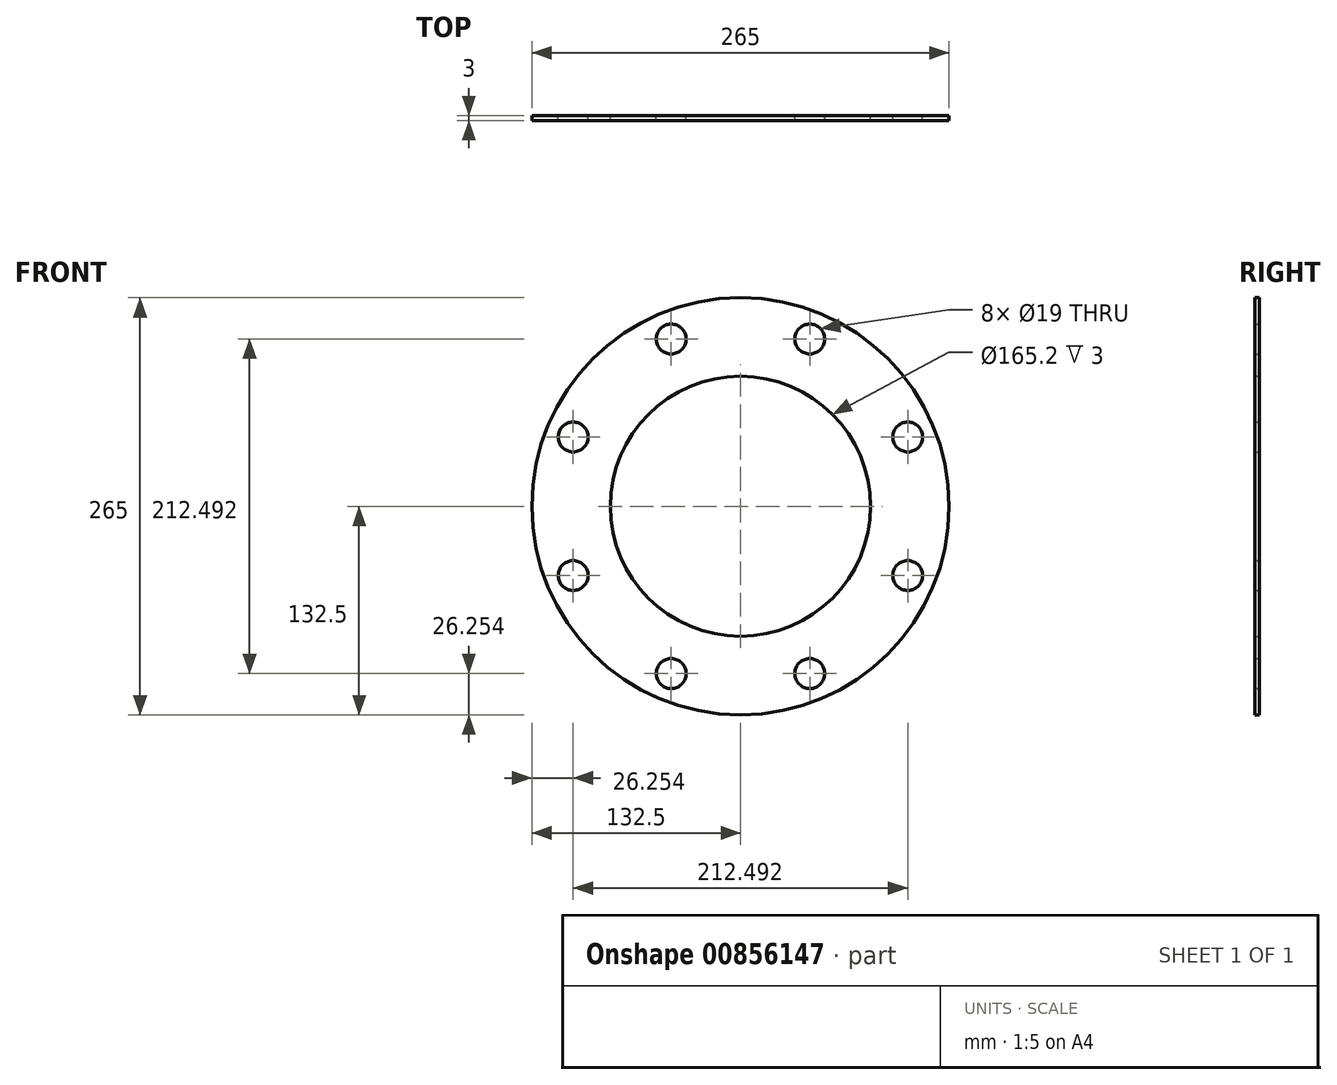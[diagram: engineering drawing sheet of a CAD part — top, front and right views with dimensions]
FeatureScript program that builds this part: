
annotation { "Feature Type Name" : "Feature", "Feature Type Description" : "" }
export const myFeature = defineFeature(function(context is Context, id is Id, definition is map)
    precondition{}
    {
        {
            var Q0;
            Q0=qCreatedBy(makeId("Front.planeOp"),FACE);
            var sketch = newSketch(context, id + "F0", { "sketchPlane" : qUnion([Q0])});
            skLineSegment(sketch, "E0", {"start": v(0, -526.54) * mm, "end": v(0, -90.52) * mm, "construction": true});
            skLineSegment(sketch, "E1", {"start": v(-10.08, -242) * mm, "end": v(258.14, -242) * mm, "construction": true});
            skLineSegment(sketch, "E2.0", {"start": v(-10.08, 0) * mm, "end": v(258.14, 0) * mm, "construction": true});
            skCircle(sketch, "E3", {"center": v(0, 0) * mm, "radius": 132.5 * mm});
            skCircle(sketch, "E4", {"center": v(0, 0) * mm, "radius": 115 * mm, "construction": true});
            skCircle(sketch, "E5", {"center": v(0, 0) * mm, "radius": 82.6 * mm});
            skLineSegment(sketch, "E6", {"start": v(32.12, -13.3) * mm, "end": v(0, 0) * mm, "construction": true});
            skCircle(sketch, "E7", {"center": v(106.25, -44) * mm, "radius": 9.5 * mm});
            skCircle(sketch, "E8.1.0", {"center": v(106.25, 44) * mm, "radius": 9.5 * mm});
            skCircle(sketch, "E8.2.0", {"center": v(44, 106.25) * mm, "radius": 9.5 * mm});
            skCircle(sketch, "E8.3.0", {"center": v(-44, 106.25) * mm, "radius": 9.5 * mm});
            skCircle(sketch, "E8.4.0", {"center": v(-106.25, 44) * mm, "radius": 9.5 * mm});
            skCircle(sketch, "E8.5.0", {"center": v(-106.25, -44) * mm, "radius": 9.5 * mm});
            skCircle(sketch, "E8.6.0", {"center": v(-44, -106.25) * mm, "radius": 9.5 * mm});
            skCircle(sketch, "E8.7.0", {"center": v(44, -106.25) * mm, "radius": 9.5 * mm});
            skSolve(sketch);
        }
        {
            var Q0;
            Q0=makeQuery(id+"F0.imprint","IMPRINT",FACE,{"disambiguationData":[TD([[makeQuery(id+"F0.imprint","IMPRINT",EDGE,{"derivedFrom":sQuery(id+"F0.wireOp",EDGE,"E3")}),1.0]])]});
            extrude(context, id + "F1", {"entities" : qUnion([Q0]), "depth" : 3 * mm, "offsetDistance" : 25 * mm});
        }
    });
